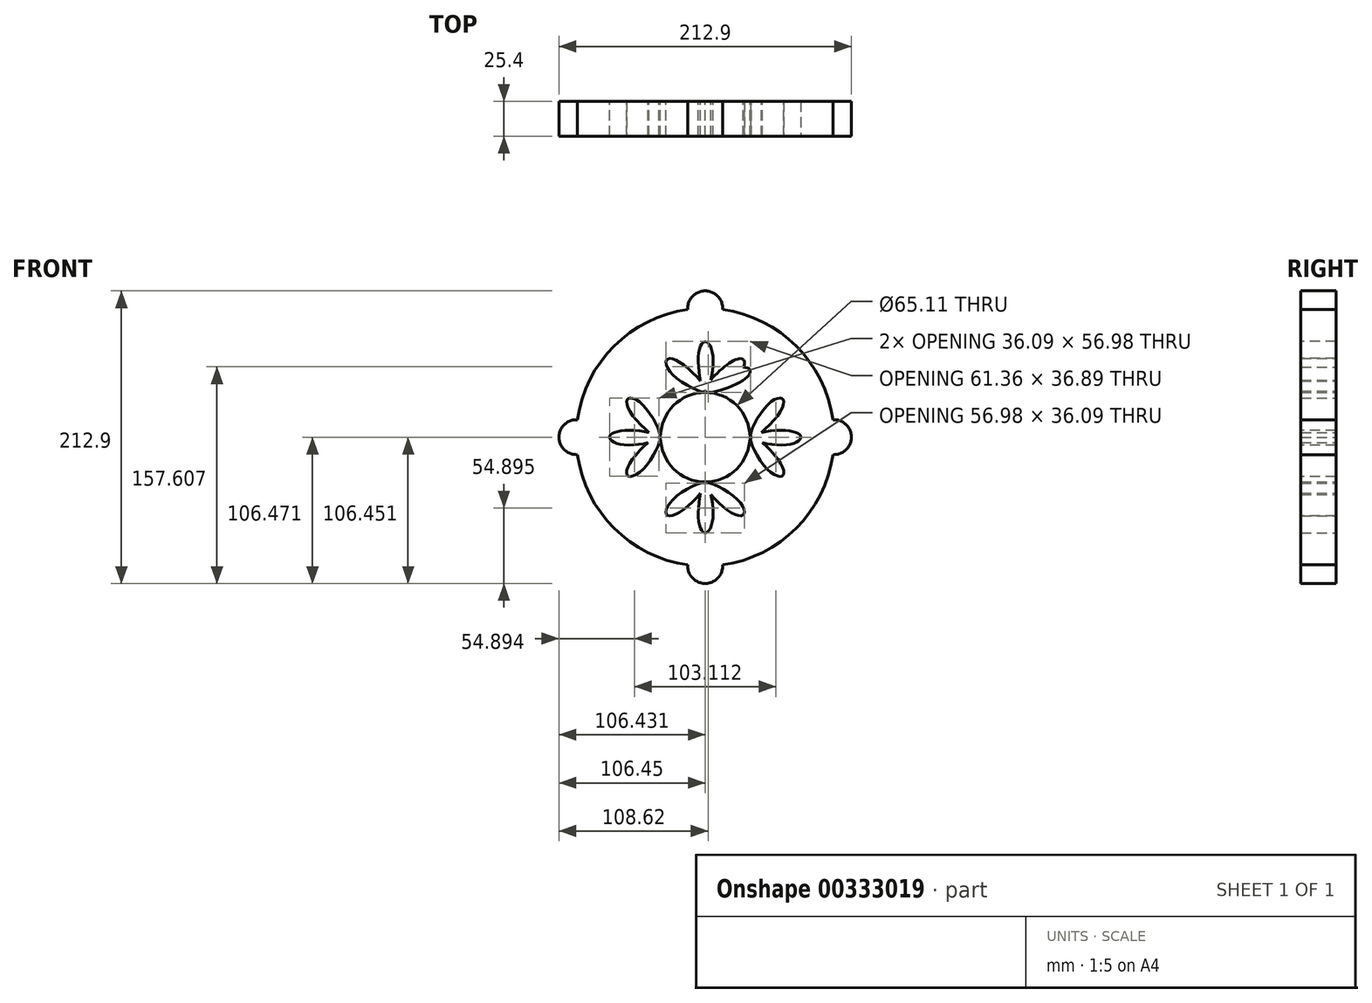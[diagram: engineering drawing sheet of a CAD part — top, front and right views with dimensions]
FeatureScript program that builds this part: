
annotation { "Feature Type Name" : "Feature", "Feature Type Description" : "" }
export const myFeature = defineFeature(function(context is Context, id is Id, definition is map)
    precondition{}
    {
        {
            var Q0;
            Q0=qCreatedBy(makeId("Front.planeOp"),FACE);
            var sketch = newSketch(context, id + "F0", { "sketchPlane" : qUnion([Q0])});
            skArc(sketch, "E0", {"start": v(1.23, 33.54) * mm, "mid": v(1.24, 33.53) * mm, "end": v(1.25, 33.51) * mm});
            skArc(sketch, "E1", {"start": v(1.23, 33.54) * mm, "mid": v(1.22, 33.53) * mm, "end": v(1.2, 33.51) * mm});
            skCircle(sketch, "E2", {"center": v(-20.2, 33.51) * mm, "radius": 93.75 * mm});
            skFitSpline(sketch, "E3", {"points": [v(-25.05, -26.03) * mm, v(-20.2, 0) * mm, v(-14.56, -25.4) * mm, v(-20.2, -36.1) * mm, v(-25.05, -26.03) * mm]});
            skPoint(sketch, "E4.endSnap0", {"position": v(-67.35, 33.51) * mm});
            skFitSpline(sketch, "E5.MirrorC", {"points": [v(-25.05, 93.06) * mm, v(-20.2, 67.02) * mm, v(-14.56, 92.43) * mm, v(-20.2, 103.11) * mm, v(-25.05, 93.06) * mm]});
            skPoint(sketch, "E6.trimOffspring.end.orphan", {"position": v(-128.68, 33.51) * mm});
            skLineSegment(sketch, "E7", {"start": v(-20.2, 67.02) * mm, "end": v(-20.28, 67.17) * mm, "construction": true});
            skFitSpline(sketch, "E8.MirrorC", {"points": [v(5.44, 73.7) * mm, v(-20.2, 67.02) * mm, v(0.4, 82.92) * mm, v(12.47, 82.38) * mm, v(5.44, 73.7) * mm]});
            skPoint(sketch, "E9.orphan", {"position": v(8.08, 111.55) * mm});
            skPoint(sketch, "E10.orphan", {"position": v(-47.72, 111.55) * mm});
            skLineSegment(sketch, "E11", {"start": v(-20.2, 67.02) * mm, "end": v(-20.36, 67.37) * mm});
            skPoint(sketch, "E12.orphan", {"position": v(-32.28, 92.43) * mm});
            skLineSegment(sketch, "E13", {"start": v(-20.2, 67.02) * mm, "end": v(-20.21, 67.07) * mm, "construction": true});
            skFitSpline(sketch, "E14.MirrorC", {"points": [v(-3.05, 87.22) * mm, v(-20.2, 67.02) * mm, v(3.07, 78.68) * mm, v(7.82, 89.79) * mm, v(-3.05, 87.22) * mm]});
            skFitSpline(sketch, "E15.MirrorC", {"points": [v(-3.05, -20.2) * mm, v(-20.2, 0) * mm, v(3.07, -11.66) * mm, v(7.82, -22.76) * mm, v(-3.05, -20.2) * mm]});
            skFitSpline(sketch, "E16.MirrorC", {"points": [v(-37.33, -20.2) * mm, v(-20.2, 0) * mm, v(-43.45, -11.66) * mm, v(-48.2, -22.76) * mm, v(-37.33, -20.2) * mm]});
            skLineSegment(sketch, "E17.trimOffspring", {"start": v(1.2, 33.51) * mm, "end": v(1.25, 33.51) * mm, "construction": true});
            skPoint(sketch, "E18.orphan", {"position": v(-20.2, 52.27) * mm});
            skFitSpline(sketch, "E19.trimOffspring", {"points": [v(-37.33, 87.22) * mm, v(-20.2, 67.02) * mm, v(-43.45, 78.68) * mm, v(-48.2, 89.79) * mm, v(-37.33, 87.22) * mm]});
            skPoint(sketch, "E20.orphan", {"position": v(-67.35, 52.27) * mm});
            skPoint(sketch, "E21.orphan", {"position": v(-67.35, 14.75) * mm});
            skPoint(sketch, "E22.orphan", {"position": v(-14.56, 14.75) * mm});
            skPoint(sketch, "E23.center.orphan", {"position": v(-49.13, -3.2) * mm});
            skPoint(sketch, "E24.bottom.end.orphan", {"position": v(-25.82, 14.75) * mm});
            skPoint(sketch, "E24.bottom.start.orphan", {"position": v(-25.05, 14.75) * mm});
            skLineSegment(sketch, "E25", {"start": v(-122.91, 33.51) * mm, "end": v(85.97, 33.51) * mm, "construction": true});
            skLineSegment(sketch, "E26", {"start": v(-20.2, 33.51) * mm, "end": v(-20.2, 178.88) * mm, "construction": true});
            skLineSegment(sketch, "E27", {"start": v(-20.2, 33.51) * mm, "end": v(-20.2, -126.77) * mm, "construction": true});
            skCircle(sketch, "E28", {"center": v(-113.94, 33.51) * mm, "radius": 12.7 * mm});
            skCircle(sketch, "E29", {"center": v(-20.2, -60.24) * mm, "radius": 12.7 * mm});
            skCircle(sketch, "E30", {"center": v(73.56, 33.51) * mm, "radius": 12.7 * mm});
            skCircle(sketch, "E31", {"center": v(-20.2, 127.26) * mm, "radius": 12.7 * mm});
            skFitSpline(sketch, "E32.MirrorCS", {"points": [v(-79.73, 38.37) * mm, v(-53.7, 33.51) * mm, v(-79.1, 27.88) * mm, v(-89.8, 33.51) * mm, v(-79.73, 38.37) * mm]});
            skFitSpline(sketch, "E33.MirrorCS", {"points": [v(-73.9, 50.65) * mm, v(-53.7, 33.51) * mm, v(-65.36, 56.77) * mm, v(-76.47, 61.52) * mm, v(-73.9, 50.65) * mm]});
            skFitSpline(sketch, "E34.MirrorCS", {"points": [v(-73.9, 16.38) * mm, v(-53.7, 33.51) * mm, v(-65.36, 10.25) * mm, v(-76.47, 5.5) * mm, v(-73.9, 16.38) * mm]});
            skFitSpline(sketch, "E35.MirrorCS", {"points": [v(39.35, 38.37) * mm, v(13.32, 33.51) * mm, v(38.73, 27.88) * mm, v(49.41, 33.51) * mm, v(39.35, 38.37) * mm]});
            skFitSpline(sketch, "E36.MirrorCS", {"points": [v(33.51, 50.65) * mm, v(13.32, 33.51) * mm, v(24.98, 56.77) * mm, v(36.09, 61.52) * mm, v(33.51, 50.65) * mm]});
            skFitSpline(sketch, "E37.MirrorCS", {"points": [v(33.51, 16.38) * mm, v(13.32, 33.51) * mm, v(24.98, 10.25) * mm, v(36.09, 5.5) * mm, v(33.51, 16.38) * mm]});
            skCircle(sketch, "E38", {"center": v(-20.2, 33.51) * mm, "radius": 32.56 * mm});
            skSolve(sketch);
        }
        {
            var Q0;
            Q0 = qSketchRegion(id + "F0", true);
            extrude(context, id + "F1", {"entities" : qUnion([Q0]), "depth" : 25.4 * mm});
        }
    });
